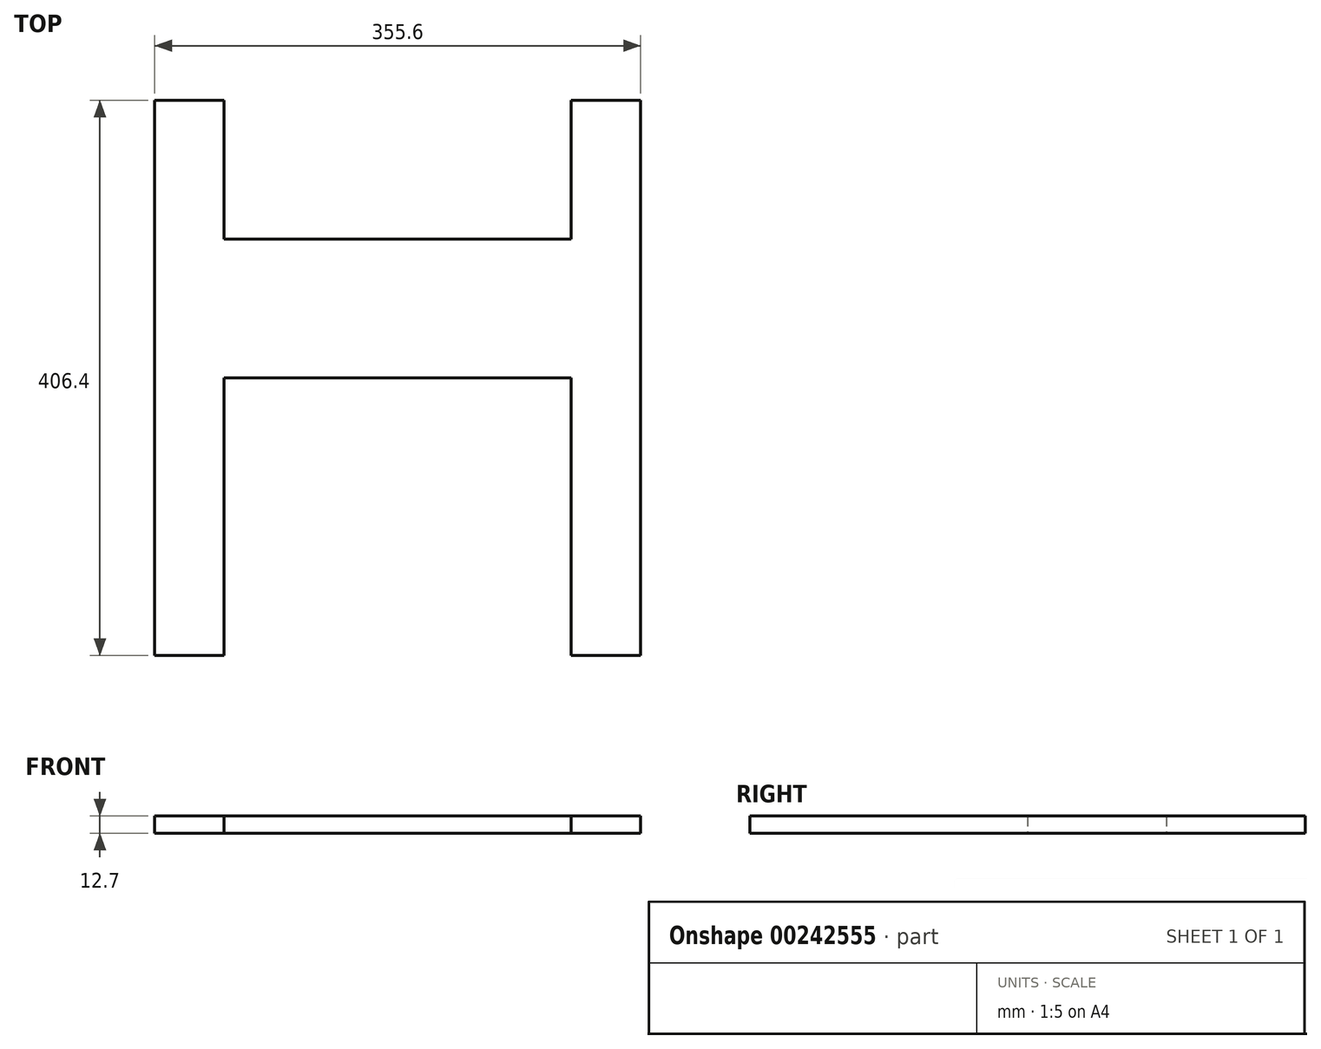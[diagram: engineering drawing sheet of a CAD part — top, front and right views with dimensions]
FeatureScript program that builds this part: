
annotation { "Feature Type Name" : "Feature", "Feature Type Description" : "" }
export const myFeature = defineFeature(function(context is Context, id is Id, definition is map)
    precondition{}
    {
        {
            var Q0;
            Q0=qCreatedBy(makeId("Top.planeOp"),FACE);
            var sketch = newSketch(context, id + "F0", { "sketchPlane" : qUnion([Q0])});
            skLineSegment(sketch, "E0.bottom", {"start": v(228.6, 228.6) * mm, "end": v(-228.6, 228.6) * mm, "construction": true});
            skLineSegment(sketch, "E0.top", {"start": v(228.6, -228.6) * mm, "end": v(-228.6, -228.6) * mm, "construction": true});
            skLineSegment(sketch, "E0.left", {"start": v(228.6, 228.6) * mm, "end": v(228.6, -228.6) * mm, "construction": true});
            skLineSegment(sketch, "E0.right", {"start": v(-228.6, 228.6) * mm, "end": v(-228.6, -228.6) * mm, "construction": true});
            skPoint(sketch, "E0.middle", {"position": v(0, 0) * mm});
            skLineSegment(sketch, "E1.bottom", {"start": v(-177.8, -177.8) * mm, "end": v(-127, -177.8) * mm});
            skLineSegment(sketch, "E1.top", {"start": v(-177.8, 228.6) * mm, "end": v(-127, 228.6) * mm});
            skLineSegment(sketch, "E1.left", {"start": v(-177.8, -177.8) * mm, "end": v(-177.8, 228.6) * mm});
            skLineSegment(sketch, "E1.right", {"start": v(-127, -177.8) * mm, "end": v(-127, 228.6) * mm});
            skLineSegment(sketch, "E2.bottom", {"start": v(177.8, -177.8) * mm, "end": v(127, -177.8) * mm});
            skLineSegment(sketch, "E2.top", {"start": v(177.8, 228.6) * mm, "end": v(127, 228.6) * mm});
            skLineSegment(sketch, "E2.left", {"start": v(177.8, -177.8) * mm, "end": v(177.8, 228.6) * mm});
            skLineSegment(sketch, "E2.right", {"start": v(127, -177.8) * mm, "end": v(127, 228.6) * mm});
            skLineSegment(sketch, "E3.bottom", {"start": v(-127, 127) * mm, "end": v(127, 127) * mm});
            skLineSegment(sketch, "E3.top", {"start": v(-127, 25.4) * mm, "end": v(127, 25.4) * mm});
            skLineSegment(sketch, "E3.left", {"start": v(-127, 127) * mm, "end": v(-127, 25.4) * mm});
            skLineSegment(sketch, "E3.right", {"start": v(127, 127) * mm, "end": v(127, 25.4) * mm});
            skSolve(sketch);
        }
        {
            var Q0;
            Q0=makeQuery(id+"F0.imprint","IMPRINT",FACE,{"disambiguationData":[TD([[makeQuery(id+"F0.imprint","IMPRINT",EDGE,{"derivedFrom":sQuery(id+"F0.wireOp",EDGE,"E3.bottom")}),-1.0]])]});
            var Q1;
            {var subQ1=sQuery(id+"F0.wireOp",EDGE,"E1.bottom");Q1=makeQuery(id+"F0.imprint","IMPRINT",FACE,{"disambiguationData":[TD([[makeQuery(id+"F0.imprint","IMPRINT",EDGE,{"derivedFrom":subQ1}),1.0]])]});}
            var Q2;
            {var subQ1=sQuery(id+"F0.wireOp",EDGE,"E2.bottom");Q2=makeQuery(id+"F0.imprint","IMPRINT",FACE,{"disambiguationData":[TD([[makeQuery(id+"F0.imprint","IMPRINT",EDGE,{"derivedFrom":subQ1}),-1.0]])]});}
            extrude(context, id + "F1", {"entities" : qUnion([Q0, Q1, Q2]), "depth" : 12.7 * mm});
        }
    });
